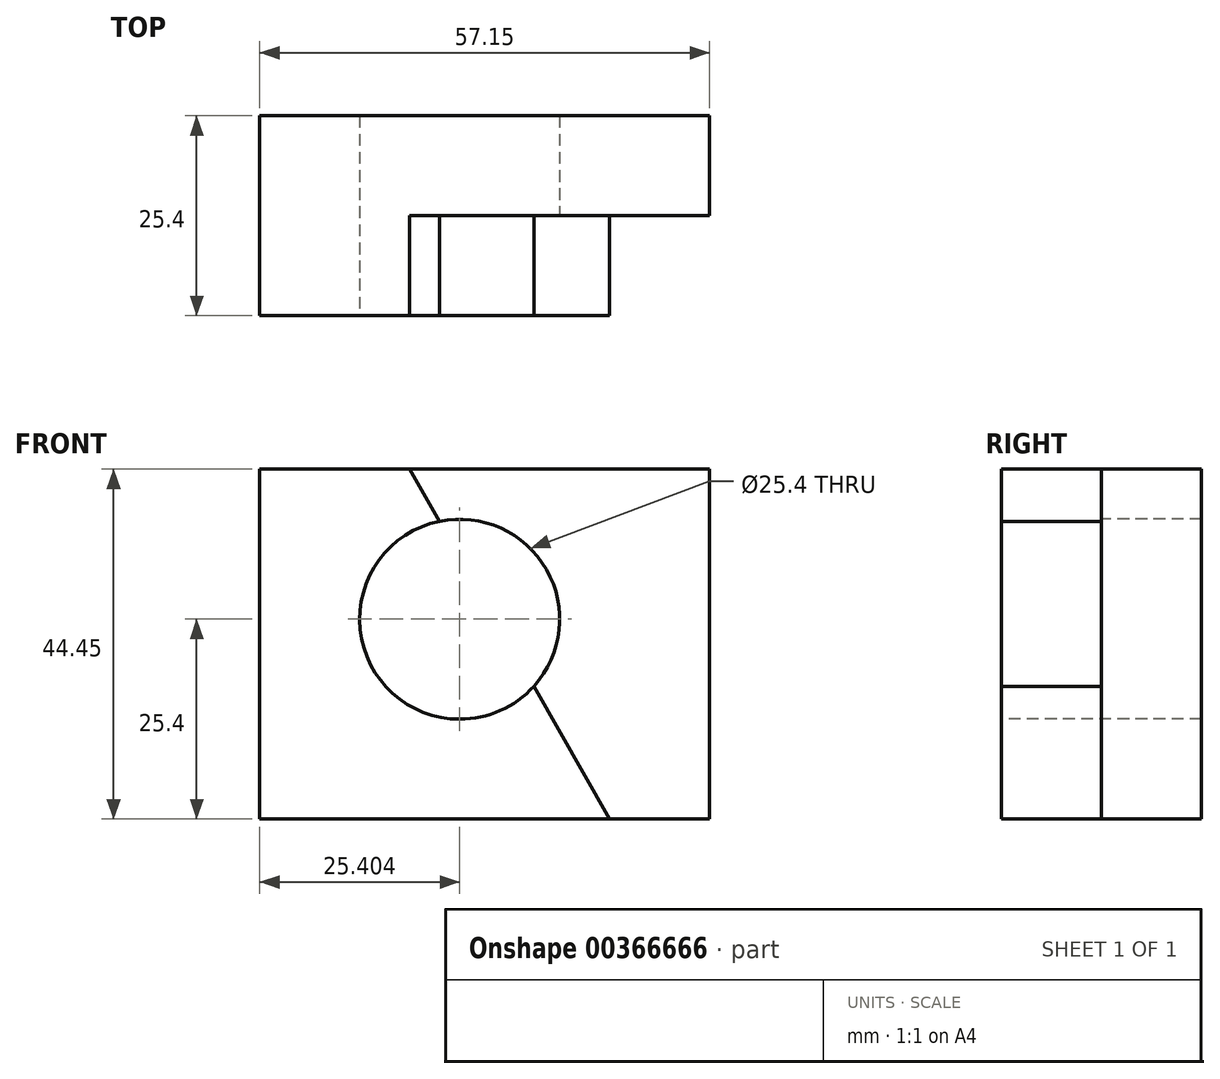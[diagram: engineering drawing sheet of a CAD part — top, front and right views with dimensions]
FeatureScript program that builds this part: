
annotation { "Feature Type Name" : "Feature", "Feature Type Description" : "" }
export const myFeature = defineFeature(function(context is Context, id is Id, definition is map)
    precondition{}
    {
        {
            var Q0;
            Q0=qCreatedBy(makeId("Front.planeOp"),FACE);
            var sketch = newSketch(context, id + "F0", { "sketchPlane" : qUnion([Q0])});
            skLineSegment(sketch, "E0", {"start": v(-69.4, 0) * mm, "end": v(-69.4, 44.45) * mm});
            skLineSegment(sketch, "E1", {"start": v(-69.4, 44.45) * mm, "end": v(-12.25, 44.45) * mm});
            skLineSegment(sketch, "E2", {"start": v(-12.25, 44.45) * mm, "end": v(-12.25, 0) * mm});
            skLineSegment(sketch, "E3", {"start": v(-12.25, 0) * mm, "end": v(-69.4, 0) * mm});
            skSolve(sketch);
        }
        {
            var Q0;
            Q0=makeQuery(id+"F0.imprint","IMPRINT",FACE,{"disambiguationData":[TD([[makeQuery(id+"F0.imprint","IMPRINT",EDGE,{"derivedFrom":sQuery(id+"F0.wireOp",EDGE,"E0")}),-1.0]])]});
            extrude(context, id + "F1", {"entities" : qUnion([Q0]), "depth" : 25.4 * mm});
        }
        {
            var Q0;
            Q0=makeQuery(id+"F1.opExtrude","CAP_FACE",FACE,{"disambiguationData":[OSD([sQuery(id+"F0.wireOp",EDGE,"E0"),sQuery(id+"F0.wireOp",EDGE,"E1"),sQuery(id+"F0.wireOp",EDGE,"E2"),sQuery(id+"F0.wireOp",EDGE,"E3")])],"isStart":false});
            var sketch = newSketch(context, id + "F2", { "sketchPlane" : qUnion([Q0])});
            skCircle(sketch, "E4", {"center": v(-44, 25.4) * mm, "radius": 12.7 * mm});
            skSolve(sketch);
        }
        {
            var Q0;
            Q0=makeQuery(id+"F2.imprint","IMPRINT",FACE,{"disambiguationData":[TD([[makeQuery(id+"F2.imprint","IMPRINT",EDGE,{"derivedFrom":sQuery(id+"F2.wireOp",EDGE,"E4")}),1.0]])]});
            extrude(context, id + "F3", {"entities" : qUnion([Q0]), "operationType" : NewBodyOperationType.REMOVE, "oppositeDirection" : true, "depth" : 25.4 * mm});
        }
        {
            var Q0;
            Q0=makeQuery(id+"F1.opExtrude","CAP_FACE",FACE,{"disambiguationData":[OSD([sQuery(id+"F0.wireOp",EDGE,"E0"),sQuery(id+"F0.wireOp",EDGE,"E1"),sQuery(id+"F0.wireOp",EDGE,"E2"),sQuery(id+"F0.wireOp",EDGE,"E3")])],"isStart":false});
            var sketch = newSketch(context, id + "F4", { "sketchPlane" : qUnion([Q0])});
            skLineSegment(sketch, "E5", {"start": v(-50.35, 44.45) * mm, "end": v(-24.95, 0) * mm});
            skSolve(sketch);
        }
        {
            var Q0;
            {var subQ0=makeQuery(id+"F1.opExtrude","CAP_EDGE",EDGE,{"disambiguationData":[OSD([sQuery(id+"F0.wireOp",EDGE,"E2")])],"isStart":false});Q0=makeQuery(id+"F4.imprint","IMPRINT",FACE,{"disambiguationData":[TD([[makeQuery(id+"F4.imprint","IMPRINT",EDGE,{"derivedFrom":subQ0}),-1.0]])]});}
            extrude(context, id + "F5", {"entities" : qUnion([Q0]), "operationType" : NewBodyOperationType.REMOVE, "oppositeDirection" : true, "depth" : 12.7 * mm});
        }
    });
